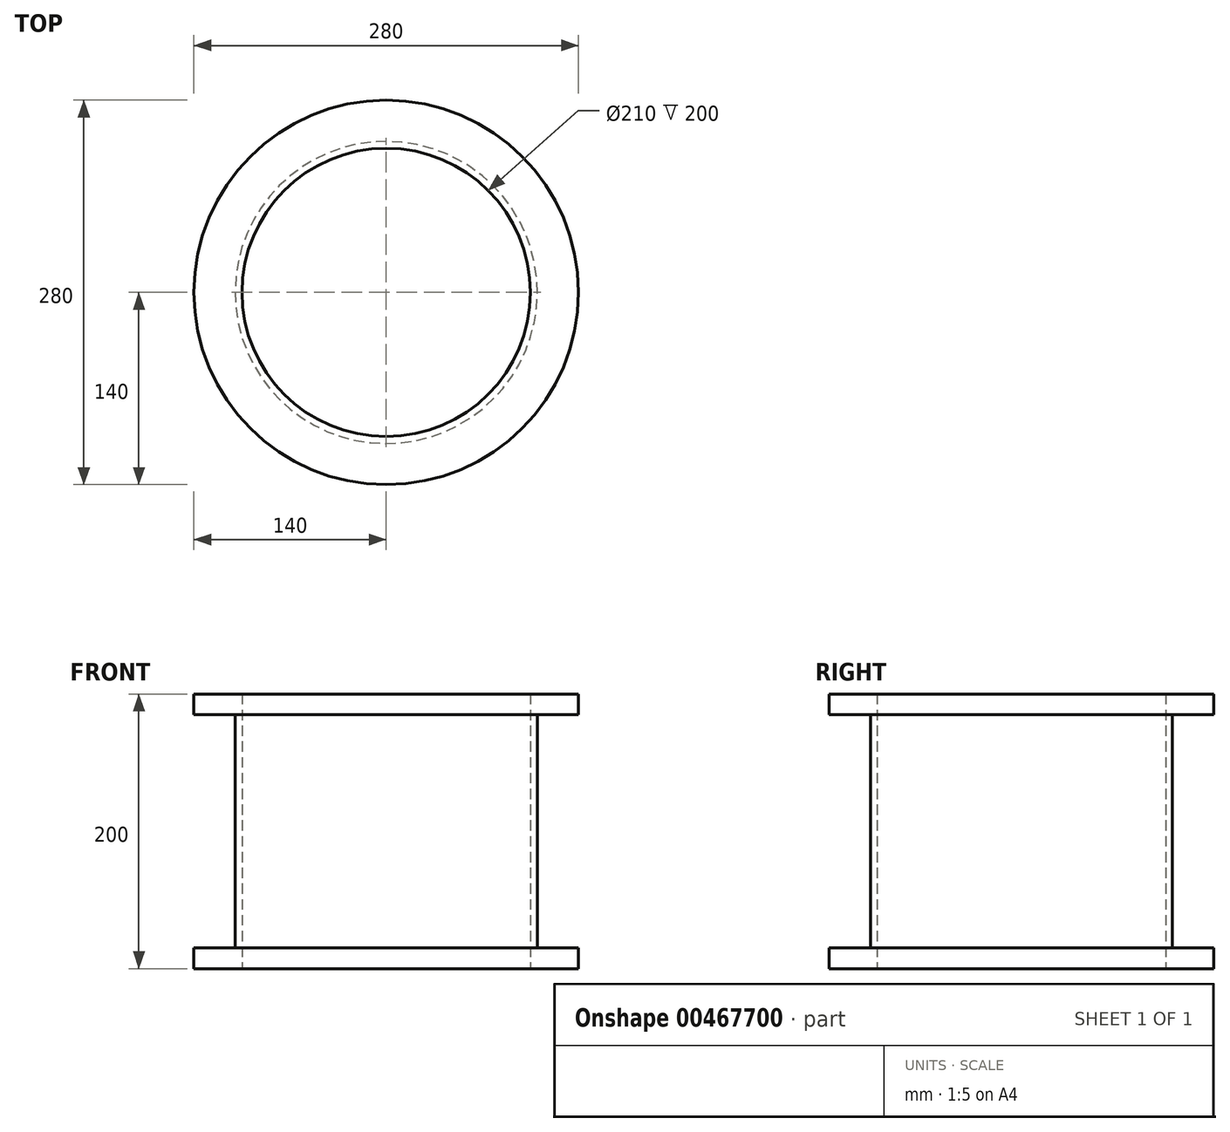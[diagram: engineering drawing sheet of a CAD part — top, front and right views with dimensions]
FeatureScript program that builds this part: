
annotation { "Feature Type Name" : "Feature", "Feature Type Description" : "" }
export const myFeature = defineFeature(function(context is Context, id is Id, definition is map)
    precondition{}
    {
        {
            var Q0;
            Q0=qCreatedBy(makeId("Front.planeOp"),FACE);
            var sketch = newSketch(context, id + "F0", { "sketchPlane" : qUnion([Q0])});
            skLineSegment(sketch, "E0", {"start": v(0, 0) * mm, "end": v(105, 0) * mm, "construction": true});
            skLineSegment(sketch, "E1", {"start": v(105, 0) * mm, "end": v(140, 0) * mm});
            skLineSegment(sketch, "E2", {"start": v(140, 0) * mm, "end": v(140, 15) * mm});
            skLineSegment(sketch, "E3", {"start": v(140, 15) * mm, "end": v(110, 15) * mm});
            skLineSegment(sketch, "E4", {"start": v(110, 15) * mm, "end": v(110, 185) * mm});
            skLineSegment(sketch, "E5", {"start": v(110, 185) * mm, "end": v(140, 185) * mm});
            skLineSegment(sketch, "E6", {"start": v(140, 185) * mm, "end": v(140, 200) * mm});
            skLineSegment(sketch, "E7", {"start": v(140, 200) * mm, "end": v(105, 200) * mm});
            skLineSegment(sketch, "E8", {"start": v(105, 200) * mm, "end": v(105, 0) * mm});
            skLineSegment(sketch, "E9", {"start": v(140, 185) * mm, "end": v(140, 15) * mm, "construction": true});
            skLineSegment(sketch, "E10", {"start": v(0, 0) * mm, "end": v(0, 197.7) * mm, "construction": true});
            skLineSegment(sketch, "E11.bottom", {"start": v(105, 200) * mm, "end": v(85, 200) * mm});
            skLineSegment(sketch, "E11.top", {"start": v(105, 0) * mm, "end": v(85, 0) * mm});
            skLineSegment(sketch, "E11.right", {"start": v(85, 200) * mm, "end": v(85, 0) * mm});
            skSolve(sketch);
        }
        {
            var Q0;
            Q0=makeQuery(id+"F0.imprint","IMPRINT",FACE,{"disambiguationData":[TD([[makeQuery(id+"F0.imprint","IMPRINT",EDGE,{"derivedFrom":sQuery(id+"F0.wireOp",EDGE,"E1")}),1.0]])]});
            var Q1;
            Q1=sQuery(id+"F0.wireOp",EDGE,"E10");
            revolve(context, id + "F1", {"entities" : qUnion([Q0]), "axis" : qUnion([Q1]), "revolveType" : RevolveType.FULL});
        }
    });
